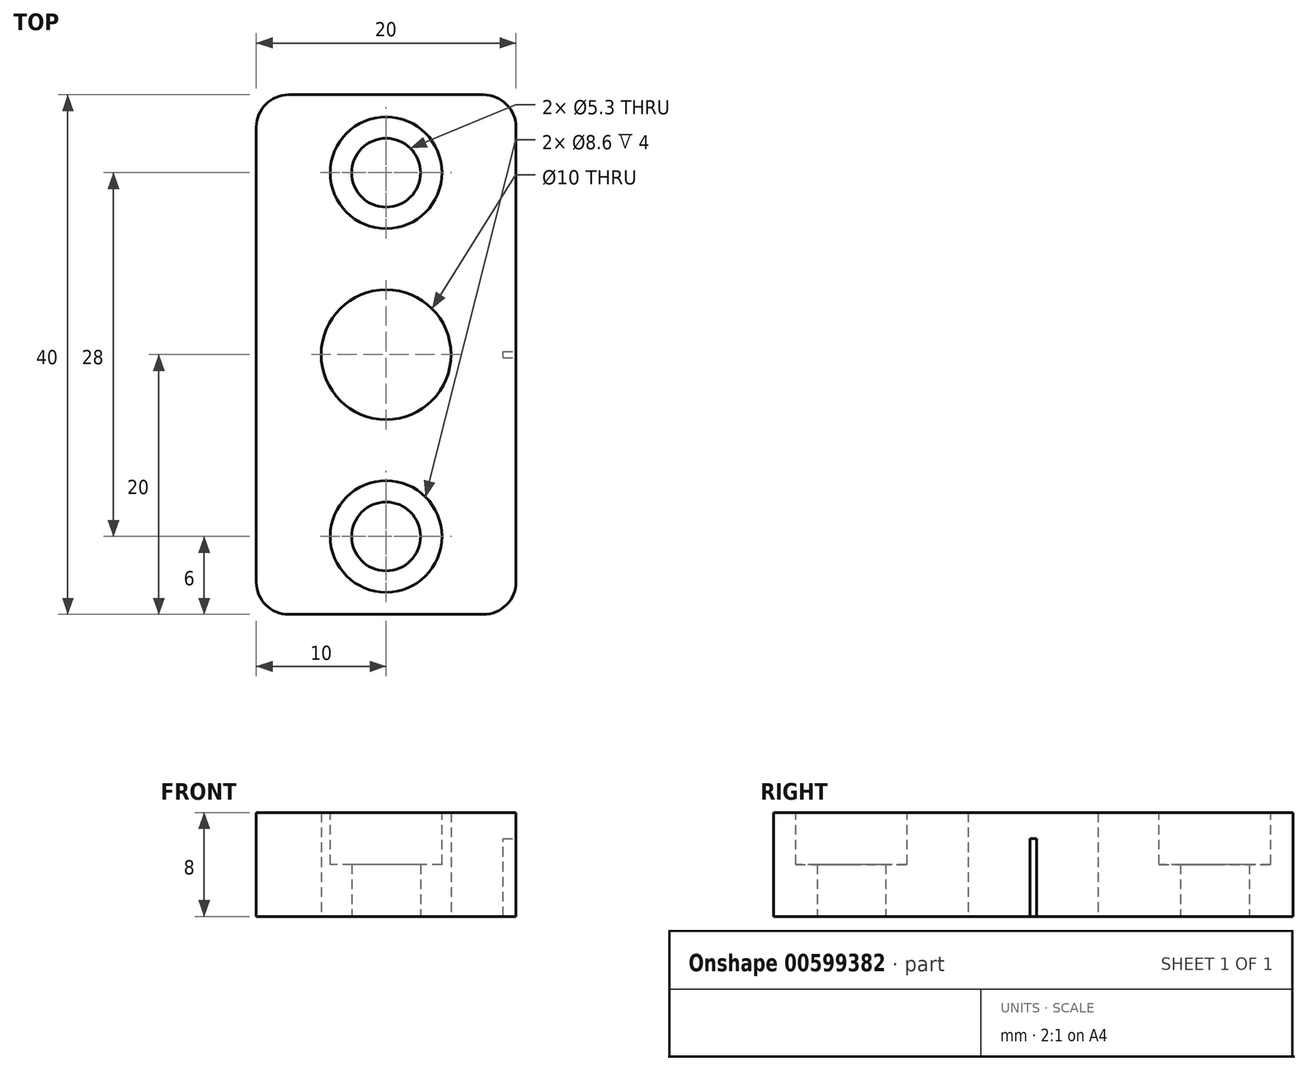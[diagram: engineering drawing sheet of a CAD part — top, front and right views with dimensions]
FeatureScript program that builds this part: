
annotation { "Feature Type Name" : "Feature", "Feature Type Description" : "" }
export const myFeature = defineFeature(function(context is Context, id is Id, definition is map)
    precondition{}
    {
        {
            var Q0;
            Q0=qCreatedBy(makeId("Top.planeOp"),FACE);
            var sketch = newSketch(context, id + "F0", { "sketchPlane" : qUnion([Q0])});
            skLineSegment(sketch, "E0.bottom", {"start": v(-10, 9) * mm, "end": v(10, 9) * mm});
            skLineSegment(sketch, "E0.top", {"start": v(-10, -9) * mm, "end": v(10, -9) * mm});
            skLineSegment(sketch, "E0.left", {"start": v(-10, 9) * mm, "end": v(-10, -9) * mm});
            skLineSegment(sketch, "E0.right", {"start": v(10, 9) * mm, "end": v(10, -9) * mm});
            skCircle(sketch, "E1", {"center": v(0, 0) * mm, "radius": 5 * mm});
            skLineSegment(sketch, "E2.bottom", {"start": v(-10, -20) * mm, "end": v(10, -20) * mm});
            skLineSegment(sketch, "E2.top", {"start": v(-10, 20) * mm, "end": v(10, 20) * mm});
            skLineSegment(sketch, "E2.left", {"start": v(-10, -20) * mm, "end": v(-10, 20) * mm});
            skLineSegment(sketch, "E2.right", {"start": v(10, -20) * mm, "end": v(10, 20) * mm});
            skCircle(sketch, "E3", {"center": v(0, 14) * mm, "radius": 2.65 * mm});
            skCircle(sketch, "E4", {"center": v(0, -14) * mm, "radius": 2.65 * mm});
            skSolve(sketch);
        }
        {
            var Q0;
            Q0=qCreatedBy(makeId("Top.planeOp"),FACE);
            var sketch = newSketch(context, id + "F1", { "sketchPlane" : qUnion([Q0])});
            skLineSegment(sketch, "E5.0", {"start": v(-10, -20) * mm, "end": v(-10, 20) * mm});
            skLineSegment(sketch, "E6.0", {"start": v(-10, -20) * mm, "end": v(10, -20) * mm});
            skLineSegment(sketch, "E7.0", {"start": v(10, -20) * mm, "end": v(10, 20) * mm});
            skLineSegment(sketch, "E8.0", {"start": v(-10, 20) * mm, "end": v(10, 20) * mm});
            skCircle(sketch, "E9.0", {"center": v(0, 14) * mm, "radius": 2.65 * mm});
            skCircle(sketch, "E10.0", {"center": v(0, -14) * mm, "radius": 2.65 * mm});
            skCircle(sketch, "E11.0", {"center": v(0, 0) * mm, "radius": 5 * mm});
            skSolve(sketch);
        }
        {
            var Q0;
            Q0=qSketchRegion(id+"F1",true);
            extrude(context, id + "F2", {"entities" : qUnion([Q0]), "depth" : 8 * mm, "offsetDistance" : 25 * mm});
        }
        {
            var Q0;
            Q0=makeQuery(id+"F2.opExtrude","CAP_FACE",FACE,{"disambiguationData":[OSD([sQuery(id+"F1.wireOp",EDGE,"E5.0"),sQuery(id+"F1.wireOp",EDGE,"E6.0"),sQuery(id+"F1.wireOp",EDGE,"E7.0"),sQuery(id+"F1.wireOp",EDGE,"E8.0"),sQuery(id+"F1.wireOp",EDGE,"E9.0"),sQuery(id+"F1.wireOp",EDGE,"E10.0"),sQuery(id+"F1.wireOp",EDGE,"E11.0")])],"isStart":false});
            var sketch = newSketch(context, id + "F3", { "sketchPlane" : qUnion([Q0])});
            skPoint(sketch, "E12", {"position": v(0, 14) * mm});
            skPoint(sketch, "E13", {"position": v(0, -14) * mm});
            skCircle(sketch, "E14", {"center": v(0, 14) * mm, "radius": 4.3 * mm});
            skCircle(sketch, "E15", {"center": v(0, -14) * mm, "radius": 4.3 * mm});
            skSolve(sketch);
        }
        {
            var Q0;
            Q0=qSketchRegion(id+"F3",true);
            extrude(context, id + "F4", {"entities" : qUnion([Q0]), "operationType" : NewBodyOperationType.REMOVE, "oppositeDirection" : true, "depth" : 4 * mm, "offsetDistance" : 25 * mm});
        }
        {
            var Q0;
            Q0=makeQuery(id+"F2.opExtrude","SWEPT_EDGE",EDGE,{"disambiguationData":[OSD([sQuery(id+"F1.wireOp",EDGE,"E6.0"),sQuery(id+"F1.wireOp",EDGE,"E7.0")])]});
            var Q1;
            Q1=makeQuery(id+"F2.opExtrude","SWEPT_EDGE",EDGE,{"disambiguationData":[OSD([sQuery(id+"F1.wireOp",EDGE,"E5.0"),sQuery(id+"F1.wireOp",EDGE,"E6.0")])]});
            var Q2;
            Q2=makeQuery(id+"F2.opExtrude","SWEPT_EDGE",EDGE,{"disambiguationData":[OSD([sQuery(id+"F1.wireOp",EDGE,"E7.0"),sQuery(id+"F1.wireOp",EDGE,"E8.0")])]});
            var Q3;
            Q3=makeQuery(id+"F2.opExtrude","SWEPT_EDGE",EDGE,{"disambiguationData":[OSD([sQuery(id+"F1.wireOp",EDGE,"E5.0"),sQuery(id+"F1.wireOp",EDGE,"E8.0")])]});
            fillet(context, id + "F5", {"entities" : qUnion([Q0, Q1, Q2, Q3]), "radius" : 2.5 * mm, "tangentPropagation" : true, "allowEdgeOverflow" : false});
        }
        {
            var Q0;
            Q0=makeQuery(id+"F2.opExtrude","SWEPT_FACE",FACE,{"disambiguationData":[OSD([sQuery(id+"F1.wireOp",EDGE,"E7.0")])]});
            var sketch = newSketch(context, id + "F6", { "sketchPlane" : qUnion([Q0])});
            skLineSegment(sketch, "E16.bottom", {"start": v(0, 0) * mm, "end": v(0.25, 0) * mm});
            skLineSegment(sketch, "E16.top", {"start": v(0, 6) * mm, "end": v(0.25, 6) * mm});
            skLineSegment(sketch, "E16.left", {"start": v(0, 0) * mm, "end": v(0, 6) * mm});
            skLineSegment(sketch, "E16.right", {"start": v(0.25, 0) * mm, "end": v(0.25, 6) * mm});
            skLineSegment(sketch, "E17.MirrorCS", {"start": v(-0.25, 0) * mm, "end": v(-0.25, 6) * mm});
            skLineSegment(sketch, "E18.MirrorCS", {"start": v(0, 6) * mm, "end": v(-0.25, 6) * mm});
            skLineSegment(sketch, "E19.MirrorCS", {"start": v(0, 0) * mm, "end": v(-0.25, 0) * mm});
            skSolve(sketch);
        }
        {
            var Q0;
            Q0=qSketchRegion(id+"F6",true);
            extrude(context, id + "F7", {"entities" : qUnion([Q0]), "operationType" : NewBodyOperationType.REMOVE, "oppositeDirection" : true, "depth" : 1 * mm});
        }
    });
